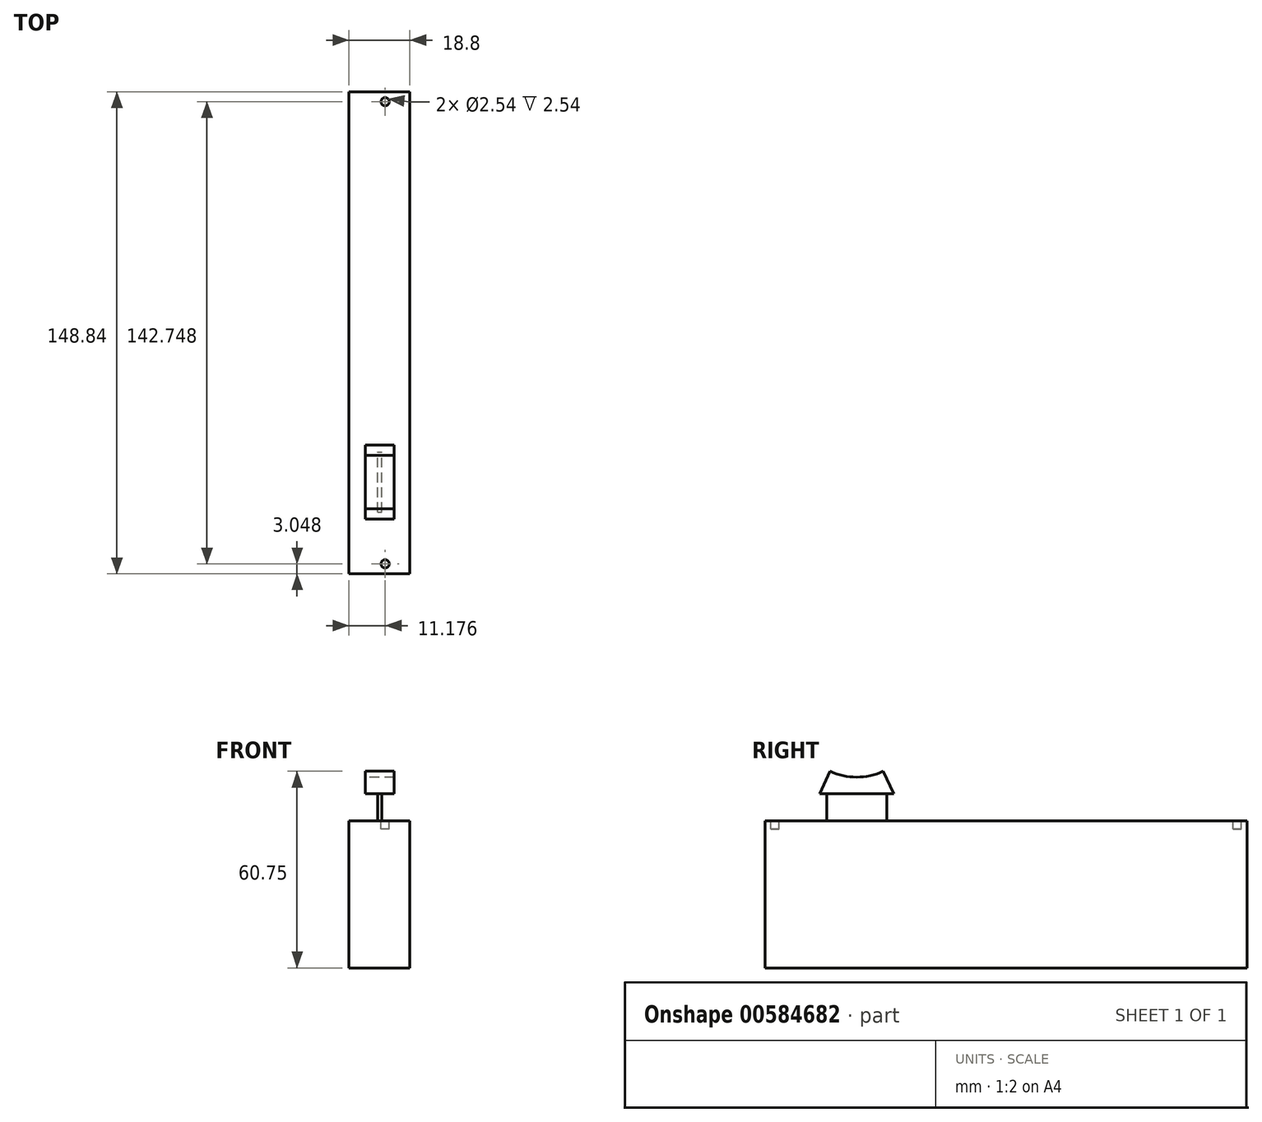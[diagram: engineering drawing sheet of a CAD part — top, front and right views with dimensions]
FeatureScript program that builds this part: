
annotation { "Feature Type Name" : "Feature", "Feature Type Description" : "" }
export const myFeature = defineFeature(function(context is Context, id is Id, definition is map)
    precondition{}
    {
        {
            var Q0;
            Q0=qCreatedBy(makeId("Right.planeOp"),FACE);
            var sketch = newSketch(context, id + "F0", { "sketchPlane" : qUnion([Q0])});
            skLineSegment(sketch, "E0.bottom", {"start": v(0, 45.47) * mm, "end": v(148.84, 45.47) * mm});
            skLineSegment(sketch, "E0.top", {"start": v(0, 0) * mm, "end": v(148.84, 0) * mm});
            skLineSegment(sketch, "E0.left", {"start": v(0, 45.47) * mm, "end": v(0, 0) * mm});
            skLineSegment(sketch, "E0.right", {"start": v(148.84, 45.47) * mm, "end": v(148.84, 0) * mm});
            skSolve(sketch);
        }
        {
            var Q0;
            Q0 = qSketchRegion(id + "F0", true);
            extrude(context, id + "F1", {"entities" : qUnion([Q0]), "depth" : 18.8 * mm, "offsetDistance" : 25.4 * mm});
        }
        {
            var Q0;
            Q0=makeQuery(id+"F1.opExtrude","SWEPT_FACE",FACE,{"disambiguationData":[OSD([sQuery(id+"F0.wireOp",EDGE,"E0.bottom")])]});
            var sketch = newSketch(context, id + "F2", { "sketchPlane" : qUnion([Q0])});
            skCircle(sketch, "E1", {"center": v(11.18, 145.8) * mm, "radius": 1.27 * mm});
            skCircle(sketch, "E2", {"center": v(11.18, 3.05) * mm, "radius": 1.27 * mm});
            skSolve(sketch);
        }
        {
            var Q0;
            Q0 = qSketchRegion(id + "F2", true);
            extrude(context, id + "F3", {"entities" : qUnion([Q0]), "operationType" : NewBodyOperationType.REMOVE, "oppositeDirection" : true, "depth" : 2.54 * mm, "offsetDistance" : 25.4 * mm});
        }
        {
            var Q0;
            Q0=qCreatedBy(makeId("Right.planeOp"),FACE);
            cPlane(context, id + "F4", {"entities" : qUnion([Q0]), "cplaneType" : CPlaneType.OFFSET, "offset" : 9.52 * mm, "width" : 152.4 * mm, "height" : 152.4 * mm});
        }
        {
            var Q0;
            Q0=qCreatedBy(id+"F4.planeOp",FACE);
            var sketch = newSketch(context, id + "F5", { "sketchPlane" : qUnion([Q0])});
            skLineSegment(sketch, "E3.bottom", {"start": v(19.05, 53.85) * mm, "end": v(37.6, 53.85) * mm});
            skLineSegment(sketch, "E3.top", {"start": v(19.05, 45.47) * mm, "end": v(37.6, 45.47) * mm});
            skLineSegment(sketch, "E3.left", {"start": v(19.05, 53.85) * mm, "end": v(19.05, 45.47) * mm});
            skLineSegment(sketch, "E3.right", {"start": v(37.6, 53.85) * mm, "end": v(37.6, 45.47) * mm});
            skSolve(sketch);
        }
        {
            var Q0;
            Q0 = qSketchRegion(id + "F5", true);
            extrude(context, id + "F6", {"entities" : qUnion([Q0]), "endBound" : BoundingType.SYMMETRIC, "oppositeDirection" : true, "depth" : 1.27 * mm, "offsetDistance" : 25.4 * mm});
        }
        {
            var Q0;
            Q0=qCreatedBy(id+"F4.planeOp",FACE);
            var sketch = newSketch(context, id + "F7", { "sketchPlane" : qUnion([Q0])});
            skLineSegment(sketch, "E4", {"start": v(16.9, 53.85) * mm, "end": v(39.75, 53.85) * mm});
            skLineSegment(sketch, "E5", {"start": v(39.75, 53.85) * mm, "end": v(36.53, 60.75) * mm});
            skLineSegment(sketch, "E6", {"start": v(16.9, 53.85) * mm, "end": v(20.11, 60.75) * mm});
            skArc(sketch, "E7", {"start": v(20.11, 60.75) * mm, "mid": v(28.32, 58.93) * mm, "end": v(36.53, 60.75) * mm});
            skSolve(sketch);
        }
        {
            var Q0;
            Q0 = qSketchRegion(id + "F7", true);
            extrude(context, id + "F8", {"entities" : qUnion([Q0]), "operationType" : NewBodyOperationType.ADD, "endBound" : BoundingType.SYMMETRIC, "depth" : 8.9 * mm, "offsetDistance" : 25.4 * mm});
        }
    });
